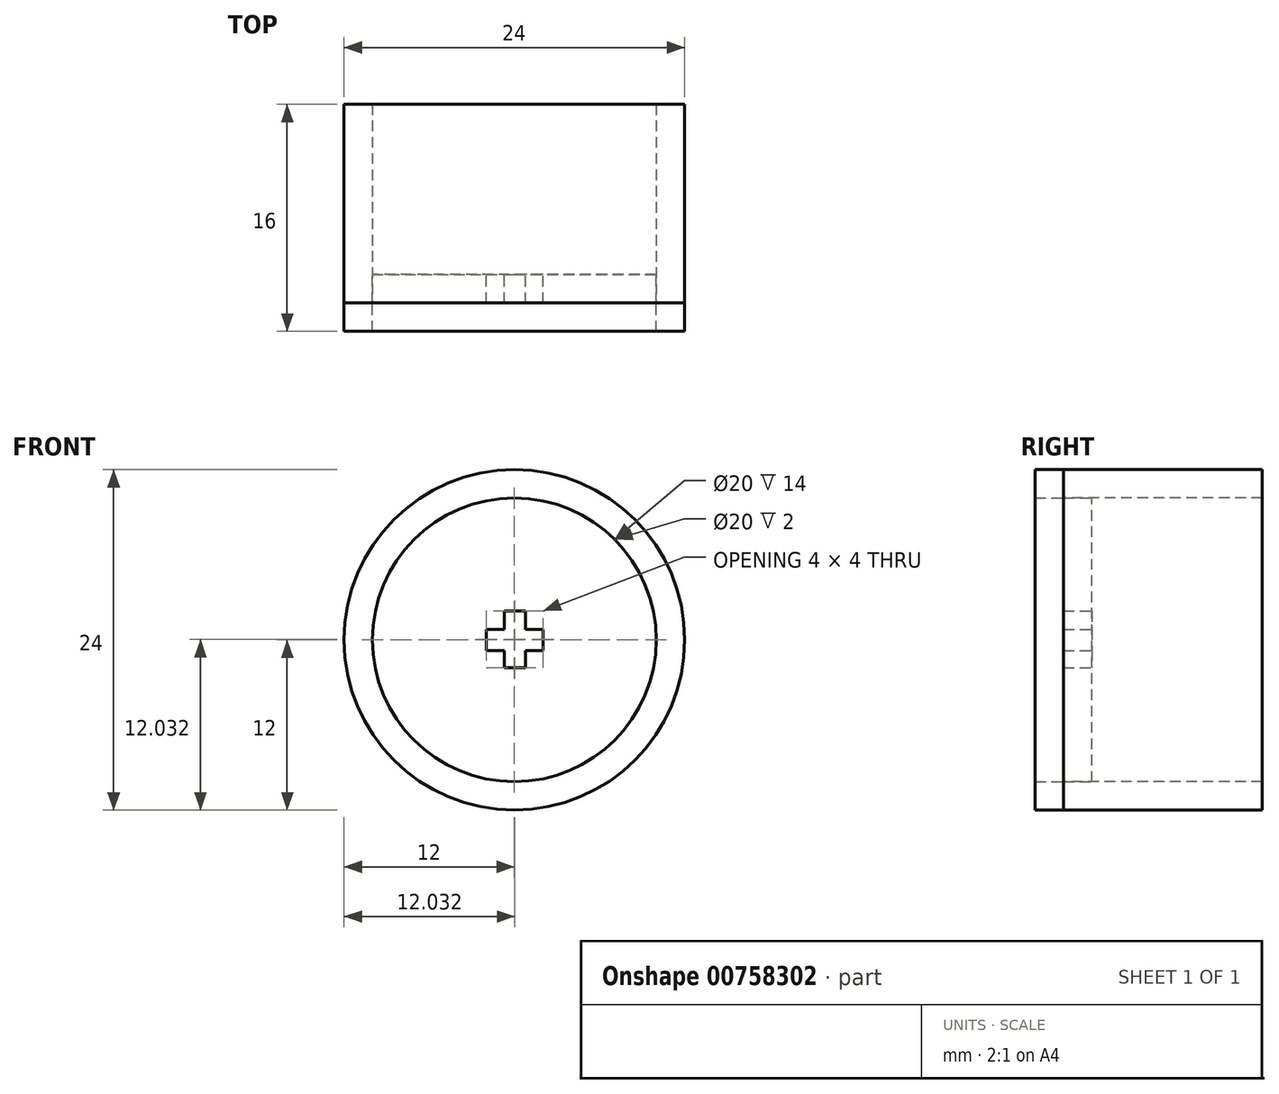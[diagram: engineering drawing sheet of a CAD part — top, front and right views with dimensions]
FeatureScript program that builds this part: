
annotation { "Feature Type Name" : "Feature", "Feature Type Description" : "" }
export const myFeature = defineFeature(function(context is Context, id is Id, definition is map)
    precondition{}
    {
        {
            var Q0;
            Q0=qCreatedBy(makeId("Front.planeOp"),FACE);
            var sketch = newSketch(context, id + "F0", { "sketchPlane" : qUnion([Q0])});
            skLineSegment(sketch, "E0", {"start": v(0.03, 2.03) * mm, "end": v(-0.72, 2.03) * mm});
            skLineSegment(sketch, "E1", {"start": v(0.03, 2.03) * mm, "end": v(0.78, 2.03) * mm});
            skLineSegment(sketch, "E2", {"start": v(-1.97, 0) * mm, "end": v(-1.97, 0.75) * mm});
            skLineSegment(sketch, "E3", {"start": v(-1.97, 0) * mm, "end": v(-1.97, -0.75) * mm});
            skLineSegment(sketch, "E4", {"start": v(0.03, -1.97) * mm, "end": v(-0.72, -1.97) * mm});
            skLineSegment(sketch, "E5", {"start": v(-0.72, -1.97) * mm, "end": v(0.03, -1.97) * mm});
            skLineSegment(sketch, "E6", {"start": v(0.03, -1.97) * mm, "end": v(0.78, -1.97) * mm});
            skLineSegment(sketch, "E7", {"start": v(2.03, 0.75) * mm, "end": v(2.03, 0) * mm});
            skLineSegment(sketch, "E8", {"start": v(2.03, 0) * mm, "end": v(2.03, -0.75) * mm});
            skLineSegment(sketch, "E9", {"start": v(-0.72, 2.03) * mm, "end": v(-0.72, 0.75) * mm});
            skLineSegment(sketch, "E10", {"start": v(0.78, 2.03) * mm, "end": v(0.78, 0.75) * mm});
            skLineSegment(sketch, "E11", {"start": v(2.03, 0.75) * mm, "end": v(0.78, 0.75) * mm});
            skLineSegment(sketch, "E12", {"start": v(-1.97, -0.75) * mm, "end": v(-0.72, -0.75) * mm});
            skLineSegment(sketch, "E13.trimOffspring", {"start": v(-0.72, 0.75) * mm, "end": v(-1.97, 0.75) * mm});
            skLineSegment(sketch, "E14.trimOffspring", {"start": v(0.78, -0.75) * mm, "end": v(2.03, -0.75) * mm});
            skLineSegment(sketch, "E15.trimOffspring", {"start": v(-0.72, -0.75) * mm, "end": v(-0.72, -1.97) * mm});
            skLineSegment(sketch, "E16.trimOffspring", {"start": v(0.78, -0.75) * mm, "end": v(0.78, -1.97) * mm});
            skCircle(sketch, "E17", {"center": v(0, 0) * mm, "radius": 10 * mm});
            skLineSegment(sketch, "E18", {"start": v(0, 0) * mm, "end": v(2.03, 0) * mm, "construction": true});
            skSolve(sketch);
        }
        {
            var Q0;
            Q0 = qSketchRegion(id + "F0", true);
            extrude(context, id + "F1", {"entities" : qUnion([Q0]), "depth" : 2 * mm, "offsetDistance" : 25.4 * mm});
        }
        {
            var Q0;
            Q0=makeQuery(id+"F1.opExtrude","CAP_FACE",FACE,{"disambiguationData":[OSD([sQuery(id+"F0.wireOp",EDGE,"E0"),sQuery(id+"F0.wireOp",EDGE,"E1"),sQuery(id+"F0.wireOp",EDGE,"E2"),sQuery(id+"F0.wireOp",EDGE,"E3"),sQuery(id+"F0.wireOp",EDGE,"E5"),sQuery(id+"F0.wireOp",EDGE,"E6"),sQuery(id+"F0.wireOp",EDGE,"E7"),sQuery(id+"F0.wireOp",EDGE,"E8"),sQuery(id+"F0.wireOp",EDGE,"E9"),sQuery(id+"F0.wireOp",EDGE,"E10"),sQuery(id+"F0.wireOp",EDGE,"E11"),sQuery(id+"F0.wireOp",EDGE,"E12"),sQuery(id+"F0.wireOp",EDGE,"E13.trimOffspring"),sQuery(id+"F0.wireOp",EDGE,"E14.trimOffspring"),sQuery(id+"F0.wireOp",EDGE,"E15.trimOffspring"),sQuery(id+"F0.wireOp",EDGE,"E16.trimOffspring"),sQuery(id+"F0.wireOp",EDGE,"E17")])],"isStart":false});
            var sketch = newSketch(context, id + "F2", { "sketchPlane" : qUnion([Q0])});
            skCircle(sketch, "E19", {"center": v(0, 0) * mm, "radius": 12 * mm});
            skCircle(sketch, "E20", {"center": v(0, 0) * mm, "radius": 10 * mm});
            skSolve(sketch);
        }
        {
            var Q0;
            Q0=makeQuery(id+"F2.imprint","IMPRINT",FACE,{"disambiguationData":[TD([[makeQuery(id+"F2.imprint","IMPRINT",EDGE,{"derivedFrom":sQuery(id+"F2.wireOp",EDGE,"E19")}),1.0]])]});
            extrude(context, id + "F3", {"entities" : qUnion([Q0]), "operationType" : NewBodyOperationType.ADD, "depth" : 2 * mm, "offsetDistance" : 25.4 * mm});
        }
        {
            var Q0;
            Q0=makeQuery(id+"F3.opExtrude","CAP_FACE",FACE,{"disambiguationData":[OSD([sQuery(id+"F2.wireOp",EDGE,"E19"),sQuery(id+"F2.wireOp",EDGE,"E20")])],"isStart":true});
            extrude(context, id + "F4", {"entities" : qUnion([Q0]), "depth" : 14 * mm, "offsetDistance" : 25.4 * mm});
        }
    });
